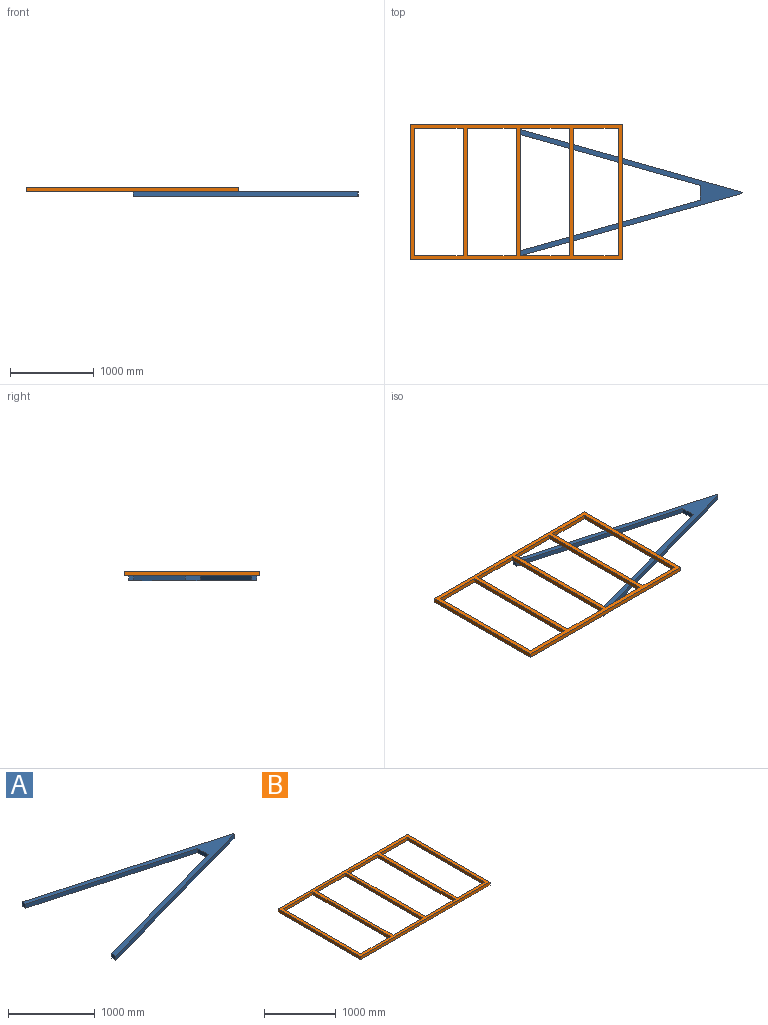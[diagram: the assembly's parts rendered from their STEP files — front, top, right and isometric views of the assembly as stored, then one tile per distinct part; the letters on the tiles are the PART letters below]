
ASSEMBLY  parts=2 mates=1
PART A: 10 faces, bbox 2689.5x1529.5x58 mm
  f0: plane 2189.72x618.67mm, normal (-0.27,-0.96,0), area 131975.4mm2, adj f1,f6,f7,f8
  f1: plane 175.22x58mm, normal (-1,0,0), area 10163mm2, adj f0,f2,f7,f8
  f2: plane 2189.72x614.25mm, normal (-0.27,0.96,0), area 131906mm2, adj f1,f3,f7,f8
  f3: plane 60.65x58mm, normal (-1,0,0), area 3517.9mm2, adj f2,f4,f7,f8
  f4: plane 2682.23x752.41mm, normal (0.27,-0.96,0), area 161574.1mm2, adj f3,f7,f8,f9
  f5: plane 2682.25x757.83mm, normal (0.27,0.96,0), area 161660.3mm2, adj f6,f7,f8,f9
  f6: plane 60.69x58mm, normal (-1,0,0), area 3519.8mm2, adj f0,f5,f7,f8
  f7: plane 2689.53x1529.48mm, normal (0,0,1), area 343577.4mm2, adj f0,f1,f2,f3,f4,f5,f6,f9
  f8: plane 2689.53x1529.48mm, normal (0,0,-1), area 343577.4mm2, adj f0,f1,f2,f3,f4,f5,f6,f9
  f9: cylinder r=10mm len=58mm, axis (0,0,-1), area 1503.8mm2, adj f4,f5,f7,f8
PART B: 22 faces, bbox 2540x1625.6x50.8 mm
  f0: plane 1524x50.8mm, normal (1,0,0), area 77419.2mm2, adj f1,f19,f20,f21
  f1: plane 533.4x50.8mm, normal (0,-1,0), area 27096.7mm2, adj f0,f2,f20,f21
  f2: plane 1524x50.8mm, normal (-1,0,0), area 77419.2mm2, adj f1,f19,f20,f21
  f3: plane 1625.6x50.8mm, normal (1,0,0), area 82580.5mm2, adj f4,f15,f20,f21
  f4: plane 2540x50.8mm, normal (0,1,0), area 129032mm2, adj f3,f5,f20,f21
  f5: plane 1625.6x50.8mm, normal (-1,0,0), area 82580.5mm2, adj f4,f15,f20,f21
  f6: plane 584.2x50.8mm, normal (0,-1,0), area 29677.4mm2, adj f7,f16,f20,f21
  f7: plane 1524x50.8mm, normal (-1,0,0), area 77419.2mm2, adj f6,f8,f20,f21
  f8: plane 584.2x50.8mm, normal (0,1,0), area 29677.4mm2, adj f7,f16,f20,f21
  f9: plane 584.2x50.8mm, normal (0,-1,0), area 29677.4mm2, adj f10,f17,f20,f21
  f10: plane 1524x50.8mm, normal (-1,0,0), area 77419.2mm2, adj f9,f11,f20,f21
  f11: plane 584.2x50.8mm, normal (0,1,0), area 29677.4mm2, adj f10,f17,f20,f21
  f12: plane 1524x50.8mm, normal (-1,0,0), area 77419.2mm2, adj f13,f18,f20,f21
  f13: plane 584.2x50.8mm, normal (0,1,0), area 29677.4mm2, adj f12,f14,f20,f21
  f14: plane 1524x50.8mm, normal (1,0,0), area 77419.2mm2, adj f13,f18,f20,f21
  f15: plane 2540x50.8mm, normal (0,-1,0), area 129032mm2, adj f3,f5,f20,f21
  f16: plane 1524x50.8mm, normal (1,0,0), area 77419.2mm2, adj f6,f8,f20,f21
  f17: plane 1524x50.8mm, normal (1,0,0), area 77419.2mm2, adj f9,f11,f20,f21
  f18: plane 584.2x50.8mm, normal (0,-1,0), area 29677.4mm2, adj f12,f14,f20,f21
  f19: plane 533.4x50.8mm, normal (0,1,0), area 27096.7mm2, adj f0,f2,f20,f21
  f20: plane 2540x1625.6mm, normal (0,0,1), area 645160mm2, adj f0,f1,f2,f3,f4,f5,f6,f7
  f21: plane 2540x1625.6mm, normal (0,0,-1), area 645160mm2, adj f0,f1,f2,f3,f4,f5,f6,f7
PLACE A t=(82.75,-107.19,-350.71)mm
PLACE B t=(72.75,-96.86,-292.71)mm
MATE fastened A.f7 <-> B.f21  axis (0,0,1) through (82.75,-838.86,-292.71)mm
